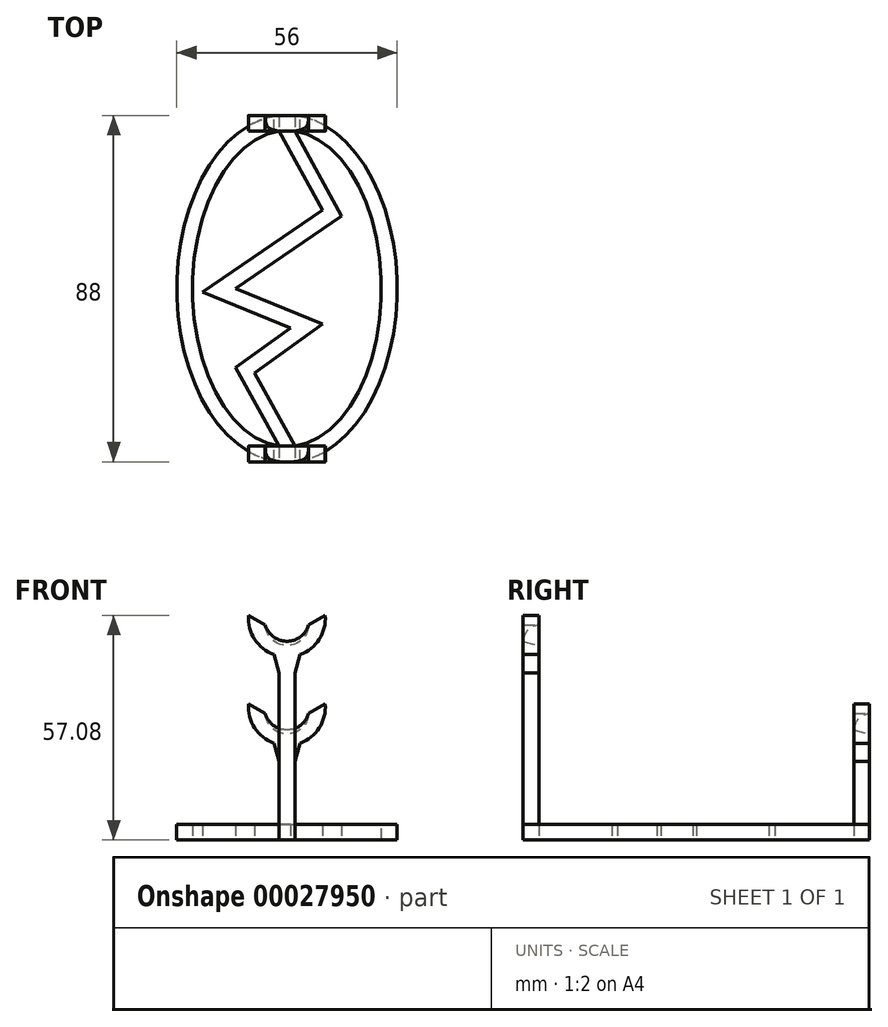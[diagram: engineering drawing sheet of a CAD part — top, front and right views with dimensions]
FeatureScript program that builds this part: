
annotation { "Feature Type Name" : "Feature", "Feature Type Description" : "" }
export const myFeature = defineFeature(function(context is Context, id is Id, definition is map)
    precondition{}
    {
        {
            var Q0;
            Q0=qCreatedBy(makeId("Right.planeOp"),FACE);
            var sketch = newSketch(context, id + "F0", { "sketchPlane" : qUnion([Q0])});
            skLineSegment(sketch, "E0.bottom", {"start": v(-44, 42.5) * mm, "end": v(-40, 42.5) * mm});
            skLineSegment(sketch, "E0.top", {"start": v(-44, 0) * mm, "end": v(-40, 0) * mm});
            skLineSegment(sketch, "E0.left", {"start": v(-44, 42.5) * mm, "end": v(-44, 0) * mm});
            skLineSegment(sketch, "E0.right", {"start": v(-40, 42.5) * mm, "end": v(-40, 0) * mm});
            skLineSegment(sketch, "E1.bottom", {"start": v(40, 20) * mm, "end": v(44, 20) * mm});
            skLineSegment(sketch, "E1.top", {"start": v(40, 0) * mm, "end": v(44, 0) * mm});
            skLineSegment(sketch, "E1.left", {"start": v(40, 20) * mm, "end": v(40, 0) * mm});
            skLineSegment(sketch, "E1.right", {"start": v(44, 20) * mm, "end": v(44, 0) * mm});
            skLineSegment(sketch, "E2", {"start": v(-40, 42.5) * mm, "end": v(44, 20) * mm, "construction": true});
            skLineSegment(sketch, "E3", {"start": v(-40, 0) * mm, "end": v(40, 0) * mm, "construction": true});
            skSolve(sketch);
        }
        {
            var Q0;
            Q0 = qSketchRegion(id + "F0", true);
            extrude(context, id + "F1", {"entities" : qUnion([Q0]), "depth" : 4 * mm});
        }
        {
            var Q0;
            Q0=qCreatedBy(makeId("Top.planeOp"),FACE);
            var sketch = newSketch(context, id + "F2", { "sketchPlane" : qUnion([Q0])});
            skLineSegment(sketch, "E4.bottom", {"start": v(0, 40) * mm, "end": v(4, 40) * mm, "construction": true});
            skLineSegment(sketch, "E4.top", {"start": v(0, -40) * mm, "end": v(4, -40) * mm, "construction": true});
            skLineSegment(sketch, "E4.left", {"start": v(0, 40) * mm, "end": v(0, -40) * mm, "construction": true});
            skLineSegment(sketch, "E4.right", {"start": v(4, 40) * mm, "end": v(4, -40) * mm, "construction": true});
            skLineSegment(sketch, "E5", {"start": v(0, 40) * mm, "end": v(11.07, 20) * mm});
            skLineSegment(sketch, "E6", {"start": v(11.07, 20) * mm, "end": v(-19.46, -0.9) * mm});
            skLineSegment(sketch, "E7", {"start": v(-19.46, -0.9) * mm, "end": v(2.86, -10) * mm});
            skLineSegment(sketch, "E8", {"start": v(2.86, -10) * mm, "end": v(-11.07, -20) * mm});
            skLineSegment(sketch, "E9", {"start": v(-11.07, -20) * mm, "end": v(0, -40) * mm});
            skLineSegment(sketch, "E10", {"start": v(4, -40) * mm, "end": v(-6.25, -21.47) * mm});
            skLineSegment(sketch, "E11", {"start": v(-6.25, -21.47) * mm, "end": v(11.07, -9.03) * mm});
            skLineSegment(sketch, "E12", {"start": v(11.07, -9.03) * mm, "end": v(-11.07, 0) * mm});
            skLineSegment(sketch, "E13", {"start": v(-11.07, 0) * mm, "end": v(15.91, 18.47) * mm});
            skLineSegment(sketch, "E14", {"start": v(15.91, 18.47) * mm, "end": v(4, 40) * mm});
            skLineSegment(sketch, "E15", {"start": v(-11.07, -20) * mm, "end": v(-11.07, 0) * mm, "construction": true});
            skLineSegment(sketch, "E16", {"start": v(11.07, 20) * mm, "end": v(11.07, -9.03) * mm, "construction": true});
            skEllipse(sketch, "E17", {"center": v(2, 0) * mm, "majorRadius": 44.11 * mm, "minorRadius": 28 * mm, "majorAxis": v(0, -1)});
            skEllipse(sketch, "E18", {"center": v(2, 0) * mm, "majorRadius": 40.14 * mm, "minorRadius": 24 * mm, "majorAxis": v(0, -1)});
            skLineSegment(sketch, "E19.bottom", {"start": v(0, -40) * mm, "end": v(4, -40) * mm});
            skLineSegment(sketch, "E19.top", {"start": v(0, -44) * mm, "end": v(4, -44) * mm});
            skLineSegment(sketch, "E19.left", {"start": v(0, -40) * mm, "end": v(0, -44) * mm});
            skLineSegment(sketch, "E19.right", {"start": v(4, -40) * mm, "end": v(4, -44) * mm});
            skLineSegment(sketch, "E20.bottom", {"start": v(0, 40) * mm, "end": v(4, 40) * mm});
            skLineSegment(sketch, "E20.top", {"start": v(0, 44) * mm, "end": v(4, 44) * mm});
            skLineSegment(sketch, "E20.left", {"start": v(0, 40) * mm, "end": v(0, 44) * mm});
            skLineSegment(sketch, "E20.right", {"start": v(4, 40) * mm, "end": v(4, 44) * mm});
            skLineSegment(sketch, "E21", {"start": v(30, 0) * mm, "end": v(26, 0) * mm});
            skLineSegment(sketch, "E22", {"start": v(26, 0) * mm, "end": v(2, 0) * mm});
            skSolve(sketch);
        }
        {
            var Q0;
            {var subQ1=sQuery(id+"F2.wireOp",EDGE,"E19.left");Q0=makeQuery(id+"F2.imprint","IMPRINT",FACE,{"disambiguationData":[TD([[makeQuery(id+"F2.imprint","IMPRINT",EDGE,{"derivedFrom":subQ1}),-1.0]])]});}
            var Q1;
            {var subQ1=sQuery(id+"F2.wireOp",EDGE,"E19.right");Q1=makeQuery(id+"F2.imprint","IMPRINT",FACE,{"disambiguationData":[TD([[makeQuery(id+"F2.imprint","IMPRINT",EDGE,{"derivedFrom":subQ1}),1.0]])]});}
            var Q2;
            Q2=makeQuery(id+"F2.imprint","IMPRINT",FACE,{"disambiguationData":[TD([[makeQuery(id+"F2.imprint","IMPRINT",EDGE,{"derivedFrom":sQuery(id+"F2.wireOp",EDGE,"E19.top")}),1.0]])]});
            var Q3;
            Q3=makeQuery(id+"F2.imprint","IMPRINT",FACE,{"disambiguationData":[TD([[makeQuery(id+"F2.imprint","IMPRINT",EDGE,{"derivedFrom":sQuery(id+"F2.wireOp",EDGE,"E5")}),1.0]])]});
            var Q4;
            Q4=makeQuery(id+"F2.imprint","IMPRINT",FACE,{"disambiguationData":[TD([[makeQuery(id+"F2.imprint","IMPRINT",EDGE,{"derivedFrom":sQuery(id+"F2.wireOp",EDGE,"E20.top")}),-1.0]])]});
            var Q5;
            {var subQ1=sQuery(id+"F2.wireOp",EDGE,"E20.right");Q5=makeQuery(id+"F2.imprint","IMPRINT",FACE,{"disambiguationData":[TD([[makeQuery(id+"F2.imprint","IMPRINT",EDGE,{"derivedFrom":subQ1}),-1.0]])]});}
            extrude(context, id + "F3", {"entities" : qUnion([Q0, Q1, Q2, Q3, Q4, Q5]), "operationType" : NewBodyOperationType.ADD, "depth" : 4 * mm});
        }
        {
            var Q0;
            Q0=makeQuery(id+"F1.opExtrude","SWEPT_FACE",FACE,{"disambiguationData":[OSD([sQuery(id+"F0.wireOp",EDGE,"E1.right")])]});
            var sketch = newSketch(context, id + "F4", { "sketchPlane" : qUnion([Q0])});
            skCircle(sketch, "E23", {"center": v(-2, 33.75) * mm, "radius": 5.75 * mm, "construction": true});
            skLineSegment(sketch, "E24", {"start": v(-2, 33.75) * mm, "end": v(-2, 20) * mm, "construction": true});
            skLineSegment(sketch, "E25", {"start": v(0, 20) * mm, "end": v(3.52, 32.15) * mm});
            skLineSegment(sketch, "E26", {"start": v(-4, 20) * mm, "end": v(-7.52, 32.15) * mm});
            skArc(sketch, "E27", {"start": v(-7.52, 32.15) * mm, "mid": v(-2, 28) * mm, "end": v(3.52, 32.15) * mm});
            skCircle(sketch, "E28", {"center": v(-2, 33.75) * mm, "radius": 9.75 * mm, "construction": true});
            skArc(sketch, "E29", {"start": v(-11.72, 34.57) * mm, "mid": v(-2, 24) * mm, "end": v(7.72, 34.57) * mm});
            skLineSegment(sketch, "E30", {"start": v(-11.72, 34.57) * mm, "end": v(-7.52, 32.15) * mm});
            skLineSegment(sketch, "E31", {"start": v(3.52, 32.15) * mm, "end": v(7.72, 34.57) * mm});
            skSolve(sketch);
        }
        {
            var Q0;
            {var subQ0=sQuery(id+"F0.wireOp",EDGE,"E1.right");var subQ1=makeQuery(id+"F1.opExtrude","SWEPT_EDGE",EDGE,{"disambiguationData":[OSD([sQuery(id+"F0.wireOp",EDGE,"E1.bottom"),subQ0])]});Q0=makeQuery(id+"F4.imprint","IMPRINT",FACE,{"disambiguationData":[TD([[makeQuery(id+"F4.imprint","IMPRINT",EDGE,{"derivedFrom":subQ1}),1.0]])]});}
            var Q1;
            {var subQ0=sQuery(id+"F4.wireOp",EDGE,"E30");Q1=makeQuery(id+"F4.imprint","IMPRINT",FACE,{"disambiguationData":[TD([[makeQuery(id+"F4.imprint","IMPRINT",EDGE,{"derivedFrom":subQ0}),-1.0]])]});}
            var Q2;
            {var subQ5=sQuery(id+"F4.wireOp",EDGE,"E27");Q2=makeQuery(id+"F4.imprint","IMPRINT",FACE,{"disambiguationData":[TD([[makeQuery(id+"F4.imprint","IMPRINT",EDGE,{"derivedFrom":subQ5}),-1.0]])]});}
            var Q3;
            {var subQ0=sQuery(id+"F4.wireOp",EDGE,"E31");Q3=makeQuery(id+"F4.imprint","IMPRINT",FACE,{"disambiguationData":[TD([[makeQuery(id+"F4.imprint","IMPRINT",EDGE,{"derivedFrom":subQ0}),-1.0]])]});}
            extrude(context, id + "F5", {"entities" : qUnion([Q0, Q1, Q2, Q3]), "operationType" : NewBodyOperationType.ADD, "oppositeDirection" : true, "depth" : 4 * mm});
        }
        {
            var Q0;
            Q0=makeQuery(id+"F1.opExtrude","SWEPT_FACE",FACE,{"disambiguationData":[OSD([sQuery(id+"F0.wireOp",EDGE,"E0.right")])]});
            var sketch = newSketch(context, id + "F6", { "sketchPlane" : qUnion([Q0])});
            skLineSegment(sketch, "E32", {"start": v(-2, 42.5) * mm, "end": v(-2, 56.26) * mm, "construction": true});
            skCircle(sketch, "E33", {"center": v(-2, 56.26) * mm, "radius": 5.75 * mm, "construction": true});
            skCircle(sketch, "E34", {"center": v(-2, 56.26) * mm, "radius": 9.75 * mm, "construction": true});
            skLineSegment(sketch, "E35", {"start": v(-7.52, 54.66) * mm, "end": v(-4, 42.5) * mm});
            skLineSegment(sketch, "E36", {"start": v(-4, 42.5) * mm, "end": v(0, 42.5) * mm});
            skLineSegment(sketch, "E37", {"start": v(0, 42.5) * mm, "end": v(3.52, 54.66) * mm});
            skLineSegment(sketch, "E38", {"start": v(3.52, 54.66) * mm, "end": v(7.72, 57.08) * mm});
            skLineSegment(sketch, "E39", {"start": v(-7.52, 54.66) * mm, "end": v(-11.72, 57.08) * mm});
            skArc(sketch, "E40", {"start": v(-7.52, 54.66) * mm, "mid": v(-2, 50.5) * mm, "end": v(3.52, 54.66) * mm});
            skArc(sketch, "E41", {"start": v(-11.72, 57.08) * mm, "mid": v(-2, 46.5) * mm, "end": v(7.72, 57.08) * mm});
            skSolve(sketch);
        }
        {
            var Q0;
            Q0 = qSketchRegion(id + "F6", true);
            extrude(context, id + "F7", {"entities" : qUnion([Q0]), "operationType" : NewBodyOperationType.ADD, "oppositeDirection" : true, "depth" : 4 * mm});
        }
        {
            var Q0;
            Q0=makeQuery(id+"F1.opExtrude","CAP_FACE",FACE,{"disambiguationData":[OSD([sQuery(id+"F0.wireOp",EDGE,"E0.bottom"),sQuery(id+"F0.wireOp",EDGE,"E0.top"),sQuery(id+"F0.wireOp",EDGE,"E0.left"),sQuery(id+"F0.wireOp",EDGE,"E0.right")])],"isStart":false});
            var Q1;
            Q1=makeQuery(id+"F1.opExtrude","CAP_FACE",FACE,{"disambiguationData":[OSD([sQuery(id+"F0.wireOp",EDGE,"E0.bottom"),sQuery(id+"F0.wireOp",EDGE,"E0.top"),sQuery(id+"F0.wireOp",EDGE,"E0.left"),sQuery(id+"F0.wireOp",EDGE,"E0.right")])],"isStart":true});
            cPlane(context, id + "F8", {"entities" : qUnion([Q0, Q1]), "cplaneType" : CPlaneType.MID_PLANE, "offset" : 150 * mm, "width" : 150 * mm, "height" : 150 * mm});
        }
        {
            var Q0;
            Q0=makeQuery(id+"F1.opExtrude","SWEPT_EDGE",EDGE,{"disambiguationData":[OSD([sQuery(id+"F0.wireOp",EDGE,"E1.top"),sQuery(id+"F0.wireOp",EDGE,"E1.right")])]});
            cPlane(context, id + "F9", {"entities" : qUnion([Q0]), "cplaneType" : CPlaneType.LINE_ANGLE, "offset" : 150 * mm, "angle" : 105 * degree, "width" : 150 * mm, "height" : 150 * mm});
        }
        {
            var Q0;
            Q0=qCreatedBy(id+"F9.planeOp",FACE);
            cPlane(context, id + "F10", {"entities" : qUnion([Q0]), "cplaneType" : CPlaneType.OFFSET, "offset" : 26 * mm, "width" : 150 * mm, "height" : 150 * mm});
        }
        {
            var Q0;
            Q0=qCreatedBy(id+"F8.planeOp",FACE);
            var sketch = newSketch(context, id + "F11", { "sketchPlane" : qUnion([Q0])});
            skLineSegment(sketch, "E42", {"start": v(44, 26.92) * mm, "end": v(-44, 50.5) * mm});
            skLineSegment(sketch, "E43", {"start": v(44, 26.92) * mm, "end": v(44, 50.5) * mm});
            skLineSegment(sketch, "E44", {"start": v(44, 50.5) * mm, "end": v(-44, 50.5) * mm});
            skLineSegment(sketch, "E45", {"start": v(-44, 50.5) * mm, "end": v(-44, 50.5) * mm});
            skLineSegment(sketch, "E46", {"start": v(44.65, 29.33) * mm, "end": v(43.35, 24.5) * mm});
            skSolve(sketch);
        }
        {
            var Q0;
            Q0=sQuery(id+"F11.wireOp",EDGE,"E42");
            var Q1;
            Q1=makeQuery(id+"F5.opExtrude","CAP_VERTEX",VERTEX,{"disambiguationData":[OSD([sQuery(id+"F4.wireOp",EDGE,"E26"),sQuery(id+"F4.wireOp",EDGE,"E27"),sQuery(id+"F4.wireOp",EDGE,"E30")])],"isStart":true});
            cPlane(context, id + "F12", {"entities" : qUnion([Q0, Q1]), "cplaneType" : CPlaneType.CURVE_POINT, "offset" : 150 * mm, "width" : 150 * mm, "height" : 150 * mm});
        }
        {
            var Q0;
            Q0=qCreatedBy(id+"F12.planeOp",FACE);
            var sketch = newSketch(context, id + "F13", { "sketchPlane" : qUnion([Q0])});
            skCircle(sketch, "E47", {"center": v(2, 42.93) * mm, "radius": 5.54 * mm});
            skSolve(sketch);
        }
        {
            var Q0;
            Q0=makeQuery(id+"F13.imprint","IMPRINT",FACE,{"disambiguationData":[TD([[makeQuery(id+"F13.imprint","IMPRINT",EDGE,{"derivedFrom":sQuery(id+"F13.wireOp",EDGE,"E47")}),1.0]])]});
            extrude(context, id + "F14", {"entities" : qUnion([Q0]), "operationType" : NewBodyOperationType.REMOVE, "endBound" : BoundingType.THROUGH_ALL, "depth" : 25 * mm, "hasSecondDirection" : true, "secondDirectionBound" : SecondDirectionBoundingType.THROUGH_ALL, "secondDirectionOppositeDirection" : true, "secondDirectionDepth" : 25 * mm});
        }
    });
